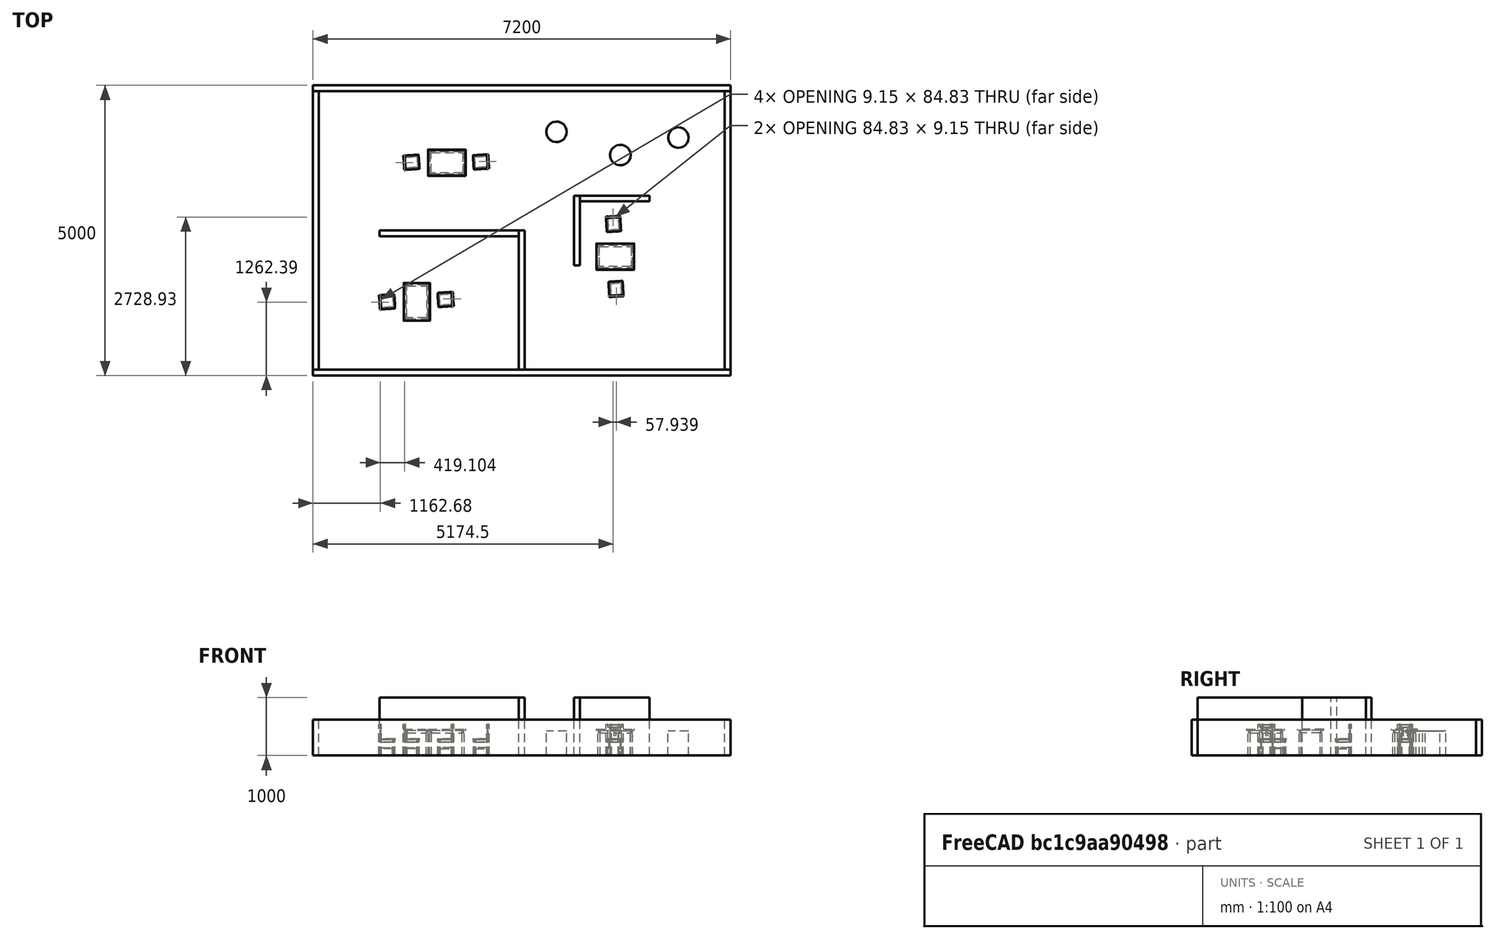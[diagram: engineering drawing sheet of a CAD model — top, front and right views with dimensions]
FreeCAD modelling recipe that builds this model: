
FCSTD DOCUMENT  (FreeCAD 0.14R2935 (Git))
Label: lucia_arena
License: CC-BY 3.0
LicenseURL: http://creativecommons.org/licenses/by/3.0/
objects: Part::MultiFuse×9, Part::Box×8, Part::Cylinder×3
note: 20 computed .brp shape members not serialized (recipe doc carries the construction recipe); baked Part::Feature solids carry a one-line shape summary decoded from their .brp

FEATURE [Part::Box] Box  label="wall_top"
  Height = 620
  Length = 7200
  Placement = pos=(0,4900,0) rot=(0,0,1;0rad)
  Width = 100
FEATURE [Part::Box] Box001  label="wall_bottom"
  Height = 620
  Length = 7200
  Width = 100
FEATURE [Part::Box] Box003  label="wall_right"
  Height = 620
  Length = 100
  Placement = pos=(7100,100,0) rot=(0,0,1;0rad)
  Width = 4800
FEATURE [Part::MultiFuse] Fusion  label="table_bl"
  Placement = pos=(1800,1200,0) rot=(0,0,1;1.5708rad)
FEATURE [Part::MultiFuse] Fusion001  label="chair_bl_l"
  Placement = pos=(1567.22,1179.83,0.000548201) rot=(0,0,1;1.5708rad)
FEATURE [Part::Box] Box004  label="wall001"
  Height = 1000
  Length = 2400
  Placement = pos=(1150,2400,0) rot=(0,0,1;0rad)
  Width = 100
FEATURE [Part::Box] Box002  label="wall_left"
  Height = 620
  Length = 100
  Placement = pos=(0,100,0) rot=(0,0,1;0rad)
  Width = 4800
FEATURE [Part::MultiFuse] Fusion002  label="chair_bl_r"
  Placement = pos=(2000,1400,0) rot=(0,0,-1;1.5708rad)
FEATURE [Part::Box] Box005  label="wall002"
  Height = 1000
  Length = 100
  Placement = pos=(3550,100,0) rot=(0,0,1;0rad)
  Width = 2400
FEATURE [Part::MultiFuse] Fusion003  label="table_br"
  Placement = pos=(5143.36,2039.72,0) rot=(0,0,1;0rad)
FEATURE [Part::MultiFuse] Fusion004  label="chair_br_l"
  Placement = pos=(5091.94,2324.39,0.00916278) rot=(0,0,1;0rad)
FEATURE [Part::MultiFuse] Fusion005  label="chair_br_r"
  Placement = pos=(5314.99,1778.31,0.00869289) rot=(0,0,1;3.14159rad)
FEATURE [Part::MultiFuse] Fusion006  label="table_tr"
  Placement = pos=(2239.94,3656.89,0.00457025) rot=(0,0,1;0rad)
FEATURE [Part::MultiFuse] Fusion007  label="chair_tr_t"
  Placement = pos=(1986.32,3585.17,-0.0016446) rot=(0,0,1;1.5708rad)
FEATURE [Part::MultiFuse] Fusion008  label="chair_tr_b"
  Placement = pos=(2609.88,3771.07,-0.00352414) rot=(0,0,-1;1.5708rad)
FEATURE [Part::Box] Box007  label="wall004"
  Height = 1000
  Length = 1200
  Placement = pos=(4600,3000,0) rot=(0,0,1;0rad)
  Width = 100
FEATURE [Part::Box] Box008  label="wall005"
  Height = 1000
  Length = 100
  Placement = pos=(4500,1900,0) rot=(0,0,1;0rad)
  Width = 1200
FEATURE [Part::Cylinder] Cylinder  label="turtlebot"
  Angle = 360
  Height = 420
  Placement = pos=(4200,4200,0.24) rot=(0,0,1;0rad)
  Radius = 177
FEATURE [Part::Cylinder] Cylinder001  label="turtlebot001"
  Angle = 360
  Height = 420
  Placement = pos=(5300,3800,0.24) rot=(0,0,1;0rad)
  Radius = 177
FEATURE [Part::Cylinder] Cylinder002  label="turtlebot002"
  Angle = 360
  Height = 420
  Placement = pos=(6300,4100,0.23) rot=(0,0,1;0rad)
  Radius = 177
